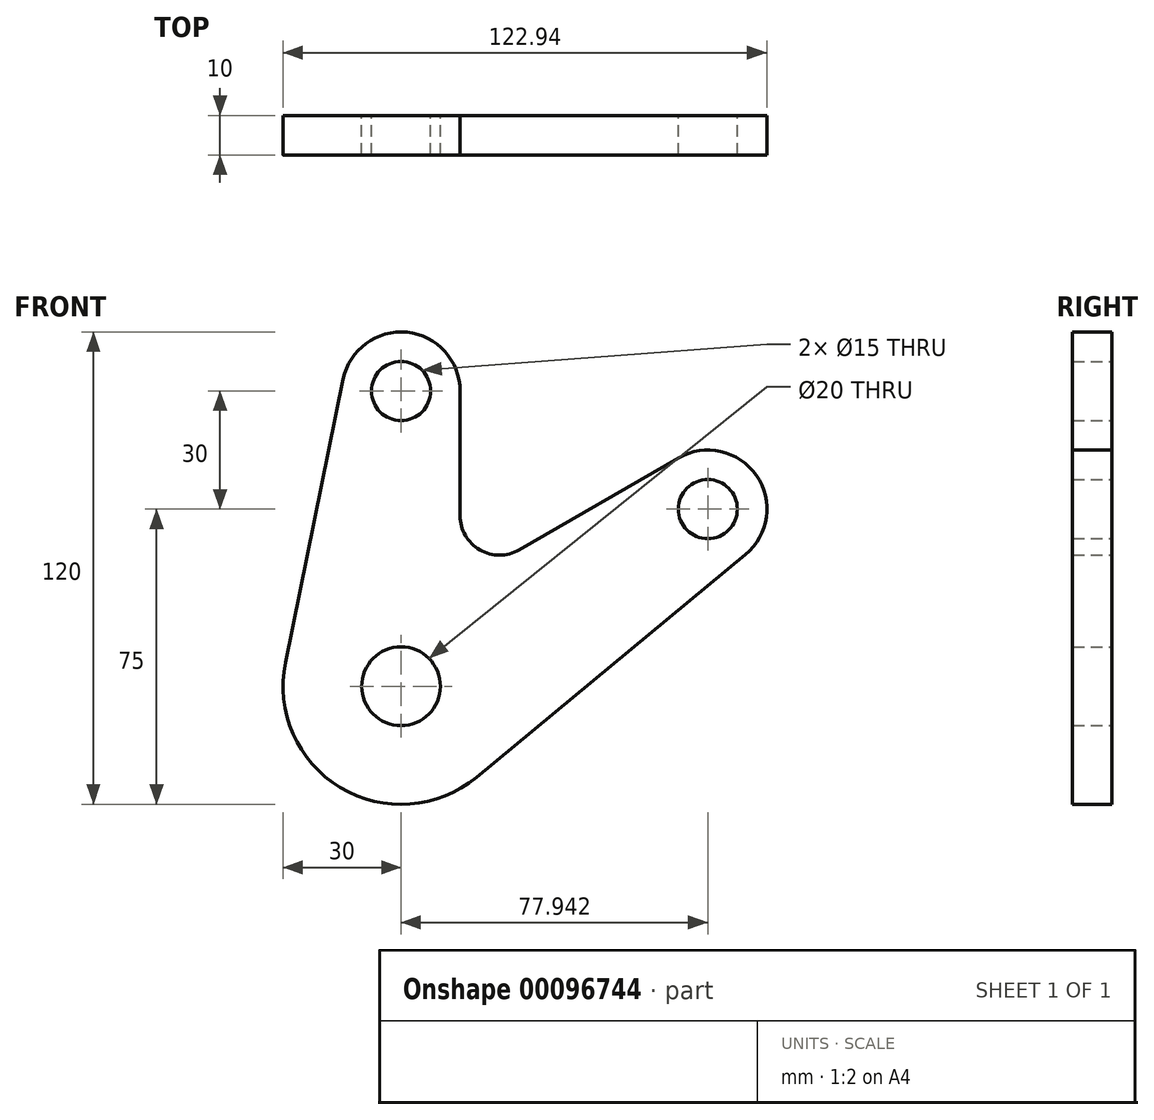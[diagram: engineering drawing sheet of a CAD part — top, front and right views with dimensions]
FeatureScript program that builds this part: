
annotation { "Feature Type Name" : "Feature", "Feature Type Description" : "" }
export const myFeature = defineFeature(function(context is Context, id is Id, definition is map)
    precondition{}
    {
        {
            var Q0;
            Q0=qCreatedBy(makeId("Front.planeOp"),FACE);
            var sketch = newSketch(context, id + "F0", { "sketchPlane" : qUnion([Q0])});
            skCircle(sketch, "E0", {"center": v(0, 0) * mm, "radius": 10 * mm});
            skLineSegment(sketch, "E1", {"start": v(15, 75) * mm, "end": v(15, 43.3) * mm});
            skLineSegment(sketch, "E2", {"start": v(30, 34.64) * mm, "end": v(70.44, 58) * mm});
            skArc(sketch, "E3", {"start": v(15, 43.3) * mm, "mid": v(20, 34.64) * mm, "end": v(30, 34.64) * mm});
            skArc(sketch, "E4", {"start": v(70.44, 58) * mm, "mid": v(90.26, 53.56) * mm, "end": v(87.5, 33.44) * mm});
            skCircle(sketch, "E5", {"center": v(77.94, 45) * mm, "radius": 7.5 * mm});
            skArc(sketch, "E6", {"start": v(-14.7, 78) * mm, "mid": v(1.5, 89.92) * mm, "end": v(15, 75) * mm});
            skCircle(sketch, "E7", {"center": v(0, 75) * mm, "radius": 7.5 * mm});
            skLineSegment(sketch, "E8", {"start": v(-14.7, 78) * mm, "end": v(-29.4, 6) * mm});
            skLineSegment(sketch, "E9", {"start": v(87.5, 33.44) * mm, "end": v(19.12, -23.12) * mm});
            skArc(sketch, "E10", {"start": v(-29.4, 6) * mm, "mid": v(-15.44, -25.72) * mm, "end": v(19.12, -23.12) * mm});
            skLineSegment(sketch, "E11", {"start": v(0, 75) * mm, "end": v(0, 0) * mm, "construction": true});
            skLineSegment(sketch, "E12", {"start": v(0, 0) * mm, "end": v(77.94, 45) * mm, "construction": true});
            skSolve(sketch);
        }
        {
            var Q0;
            Q0 = qSketchRegion(id + "F0", true);
            extrude(context, id + "F1", {"entities" : qUnion([Q0]), "depth" : 10 * mm});
        }
    });
